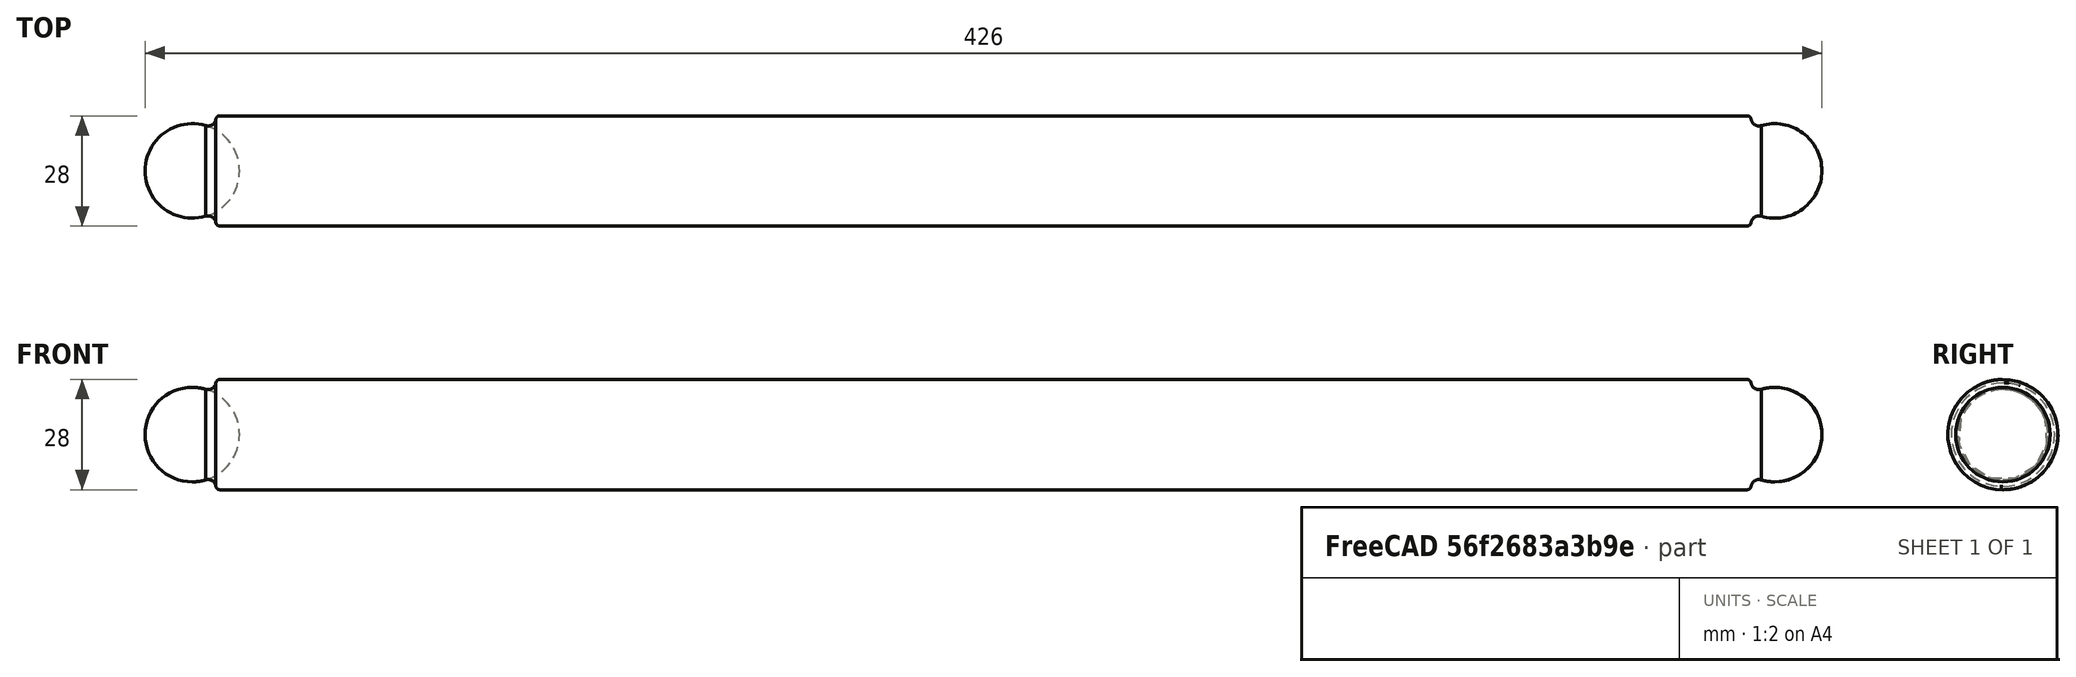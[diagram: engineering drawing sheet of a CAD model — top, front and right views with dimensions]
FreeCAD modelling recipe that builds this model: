
FCSTD DOCUMENT  (FreeCAD 0.16R6704 (Git))
Label: Object 9
License: All rights reserved
LicenseURL: http://en.wikipedia.org/wiki/All_rights_reserved
objects: Part::Sphere×2, Part::MultiFuse×2, Part::Fillet×2, Part::Cylinder×1
note: 7 computed .brp shape members not serialized (recipe doc carries the construction recipe); baked Part::Feature solids carry a one-line shape summary decoded from their .brp

FEATURE [Part::Cylinder] Cylinder041  label="barra inde001"
  Angle = 360
  Height = 390
  Placement = pos=(10,0,0) rot=(0,1,0;1.5708rad)
  Radius = 14
FEATURE [Part::Sphere] Sphere006  label="Esfera002"
  Angle1 = -90
  Angle2 = 90
  Angle3 = 360
  Placement = pos=(4,0,0) rot=(0,0,1;0rad)
  Radius = 12
FEATURE [Part::Sphere] Sphere007  label="Esfera003"
  Angle1 = -90
  Angle2 = 90
  Angle3 = 360
  Placement = pos=(406,0,0) rot=(0,0,1;0rad)
  Radius = 12
FEATURE [Part::MultiFuse] Fusion019
  Shapes = -> [Sphere006,Cylinder041]
FEATURE [Part::MultiFuse] Fusion020  label="barra independiente001"
  Placement = pos=(-450,459,261) rot=(0,0,1;0rad)
  Shapes = -> [Fusion019,Sphere007]
FEATURE [Part::Fillet] Fillet
  Base = -> Fusion020
  Edges = 3 edges r=2: [Edge4,Edge5,Edge6]
FEATURE [Part::Fillet] Fillet001
  Base = -> Fillet
  Edges = 2 edges r=1: [Edge2,Edge6]
